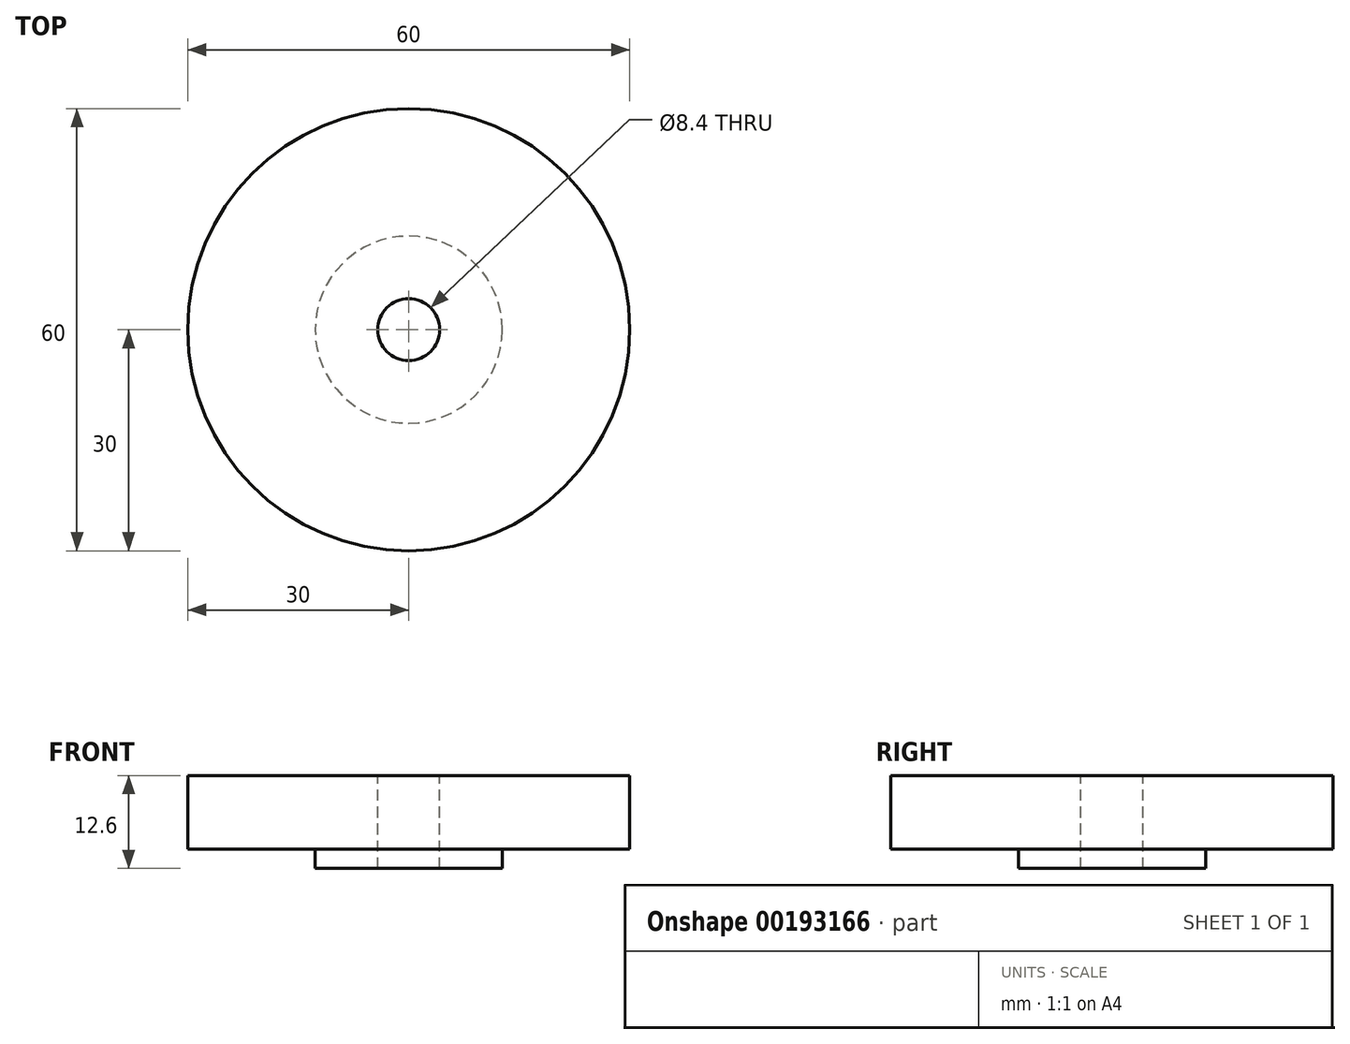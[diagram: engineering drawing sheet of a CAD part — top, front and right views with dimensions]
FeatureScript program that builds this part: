
annotation { "Feature Type Name" : "Feature", "Feature Type Description" : "" }
export const myFeature = defineFeature(function(context is Context, id is Id, definition is map)
    precondition{}
    {
        {
            var Q0;
            Q0=qCreatedBy(makeId("Top.planeOp"),FACE);
            var sketch = newSketch(context, id + "F0", { "sketchPlane" : qUnion([Q0])});
            skCircle(sketch, "E0", {"center": v(0, 0) * mm, "radius": 30 * mm});
            skCircle(sketch, "E1", {"center": v(0, 0) * mm, "radius": 16 * mm});
            skSolve(sketch);
        }
        {
            var Q0;
            Q0=makeQuery(id+"F0.imprint","IMPRINT",FACE,{"disambiguationData":[TD([[makeQuery(id+"F0.imprint","IMPRINT",EDGE,{"derivedFrom":sQuery(id+"F0.wireOp",EDGE,"E0")}),1.0]])]});
            extrude(context, id + "F1", {"entities" : qUnion([Q0]), "depth" : 10 * mm});
        }
        {
            var Q0;
            Q0=makeQuery(id+"F0.imprint","IMPRINT",FACE,{"disambiguationData":[TD([[makeQuery(id+"F0.imprint","IMPRINT",EDGE,{"derivedFrom":sQuery(id+"F0.wireOp",EDGE,"E1")}),1.0]])]});
            extrude(context, id + "F2", {"entities" : qUnion([Q0]), "operationType" : NewBodyOperationType.ADD, "depth" : 10 * mm});
        }
        {
            var Q0;
            Q0=makeQuery(id+"F0.imprint","IMPRINT",FACE,{"disambiguationData":[TD([[makeQuery(id+"F0.imprint","IMPRINT",EDGE,{"derivedFrom":sQuery(id+"F0.wireOp",EDGE,"E1")}),1.0]])]});
            var sketch = newSketch(context, id + "F3", { "sketchPlane" : qUnion([Q0])});
            skCircle(sketch, "E2", {"center": v(0, 0) * mm, "radius": 12.7 * mm});
            skSolve(sketch);
        }
        {
            var Q0;
            Q0=makeQuery(id+"F3.imprint","IMPRINT",FACE,{"disambiguationData":[TD([[makeQuery(id+"F3.imprint","IMPRINT",EDGE,{"derivedFrom":sQuery(id+"F3.wireOp",EDGE,"E2")}),1.0]])]});
            extrude(context, id + "F4", {"entities" : qUnion([Q0]), "operationType" : NewBodyOperationType.ADD, "oppositeDirection" : true, "depth" : 2.6 * mm});
        }
        {
            var Q0;
            Q0=sQuery(id+"F0.wireOp",VERTEX,"E0.center");
            var Q1;
            Q1=makeQuery(id+"F1.opExtrude","SWEPT_BODY",BODY,{"disambiguationData":[OSD([sQuery(id+"F0.wireOp",EDGE,"E0"),sQuery(id+"F0.wireOp",EDGE,"E1")])]});
            hole(context, id + "F5", {"style" : HoleStyle.SIMPLE, "endStyle" : HoleEndStyle.THROUGH, "standardTappedOrClearance" : lookupTablePath({ "standard" : "ISO", "fit" : "Close", "size" : "M8", "type" : "Clearance" }), "standardBlindInLast" : lookupTablePath({ "fit" : "Close", "standard" : "ISO", "size" : "M8", "type" : "Clearance" }), "holeDiameter" : 8.4 * mm, "locations" : qUnion([Q0]), "scope" : qUnion([Q1]), "isTappedThrough" : true});
        }
        {
            var Q0;
            Q0=sQuery(id+"F0.wireOp",VERTEX,"E0.center");
            var Q1;
            Q1=makeQuery(id+"F1.opExtrude","SWEPT_BODY",BODY,{"disambiguationData":[OSD([sQuery(id+"F0.wireOp",EDGE,"E0"),sQuery(id+"F0.wireOp",EDGE,"E1")])]});
            hole(context, id + "F6", {"style" : HoleStyle.SIMPLE, "endStyle" : HoleEndStyle.THROUGH, "oppositeDirection" : true, "standardTappedOrClearance" : lookupTablePath({ "standard" : "ISO", "fit" : "Close", "size" : "M8", "type" : "Clearance" }), "standardBlindInLast" : lookupTablePath({ "fit" : "Close", "standard" : "ISO", "size" : "M8", "type" : "Clearance" }), "holeDiameter" : 8.4 * mm, "locations" : qUnion([Q0]), "scope" : qUnion([Q1]), "isTappedThrough" : true});
        }
    });
